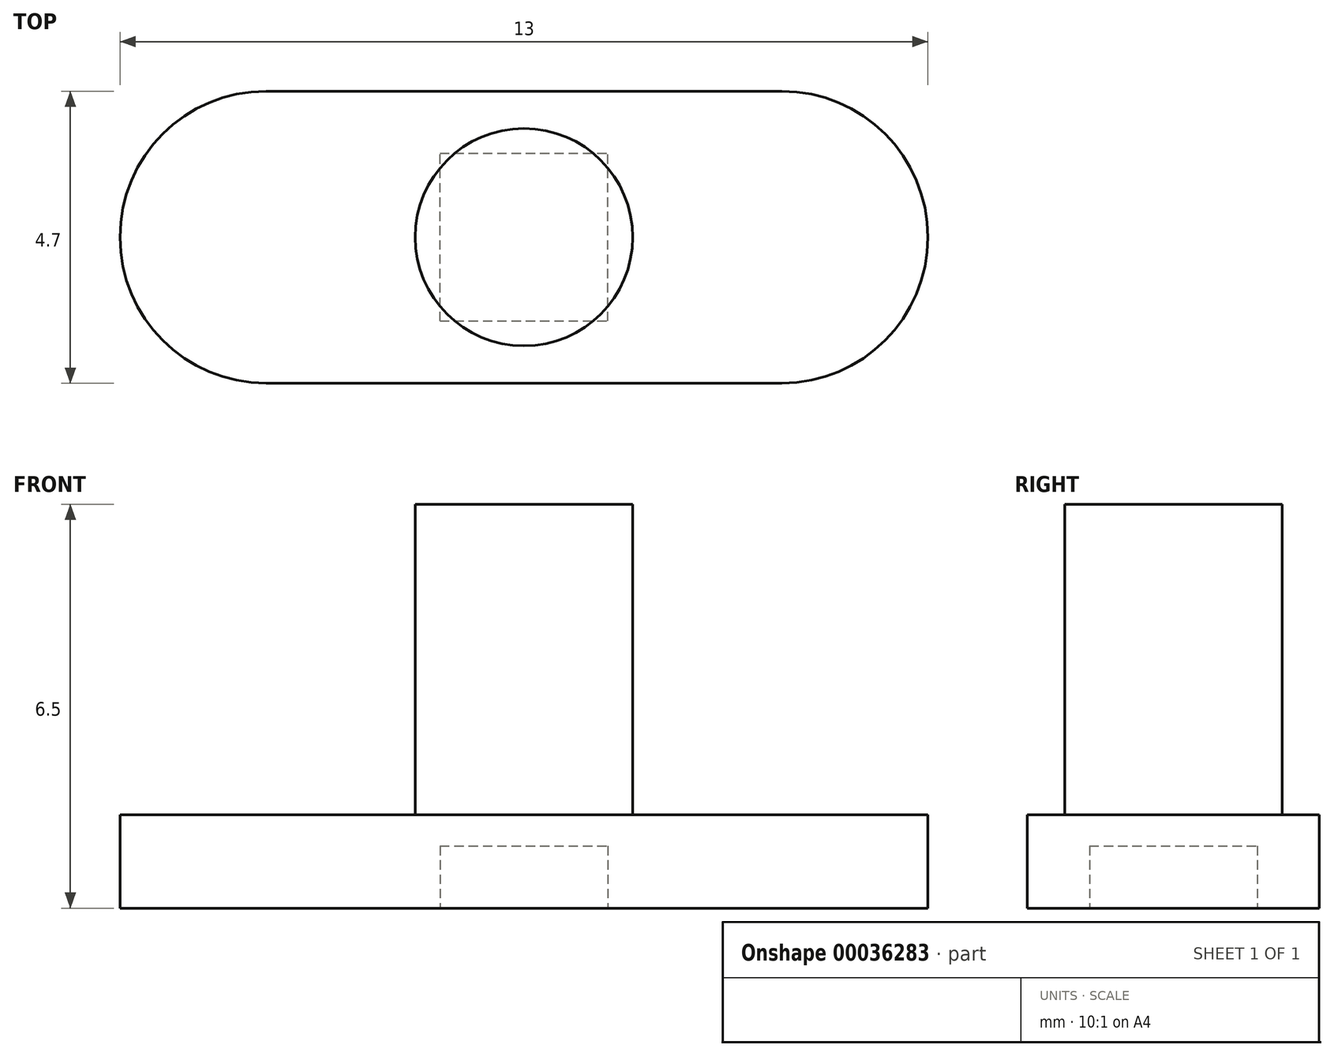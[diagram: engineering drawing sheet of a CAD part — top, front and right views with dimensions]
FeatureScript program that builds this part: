
annotation { "Feature Type Name" : "Feature", "Feature Type Description" : "" }
export const myFeature = defineFeature(function(context is Context, id is Id, definition is map)
    precondition{}
    {
        {
            var Q0;
            Q0=qCreatedBy(makeId("Top.planeOp"),FACE);
            var sketch = newSketch(context, id + "F0", { "sketchPlane" : qUnion([Q0])});
            skLineSegment(sketch, "E0.bottom", {"start": v(-0.65, 0) * mm, "end": v(7.65, 0) * mm});
            skLineSegment(sketch, "E0.top", {"start": v(-0.65, -4.7) * mm, "end": v(7.65, -4.7) * mm});
            skLineSegment(sketch, "E0.left", {"start": v(-0.65, 0) * mm, "end": v(-0.65, -4.7) * mm});
            skLineSegment(sketch, "E0.right", {"start": v(7.65, 0) * mm, "end": v(7.65, -4.7) * mm});
            skCircle(sketch, "E1", {"center": v(-0.65, -2.35) * mm, "radius": 2.35 * mm});
            skCircle(sketch, "E2", {"center": v(7.65, -2.35) * mm, "radius": 2.35 * mm});
            skLineSegment(sketch, "E3", {"start": v(-3, -2.35) * mm, "end": v(-0.65, -2.35) * mm, "construction": true});
            skLineSegment(sketch, "E4", {"start": v(-0.65, -2.35) * mm, "end": v(1.7, -2.35) * mm, "construction": true});
            skLineSegment(sketch, "E5", {"start": v(1.7, -2.35) * mm, "end": v(5.3, -2.35) * mm, "construction": true});
            skLineSegment(sketch, "E6", {"start": v(5.3, -2.35) * mm, "end": v(7.65, -2.35) * mm, "construction": true});
            skLineSegment(sketch, "E7", {"start": v(7.65, -2.35) * mm, "end": v(10, -2.35) * mm, "construction": true});
            skLineSegment(sketch, "E8", {"start": v(3.5, 0) * mm, "end": v(3.5, -2.35) * mm, "construction": true});
            skLineSegment(sketch, "E9", {"start": v(3.5, -4.7) * mm, "end": v(3.5, -2.35) * mm, "construction": true});
            skSolve(sketch);
        }
        {
            var Q0;
            {var subQ1=sQuery(id+"F0.wireOp",EDGE,"E0.left");Q0=makeQuery(id+"F0.imprint","IMPRINT",FACE,{"disambiguationData":[TD([[makeQuery(id+"F0.imprint","IMPRINT",EDGE,{"derivedFrom":subQ1}),-1.0]])]});}
            var Q1;
            {var subQ1=sQuery(id+"F0.wireOp",EDGE,"E0.left");Q1=makeQuery(id+"F0.imprint","IMPRINT",FACE,{"disambiguationData":[TD([[makeQuery(id+"F0.imprint","IMPRINT",EDGE,{"derivedFrom":subQ1}),1.0]])]});}
            var Q2;
            {var subQ3=sQuery(id+"F0.wireOp",EDGE,"E0.bottom");Q2=makeQuery(id+"F0.imprint","IMPRINT",FACE,{"disambiguationData":[TD([[makeQuery(id+"F0.imprint","IMPRINT",EDGE,{"derivedFrom":subQ3}),-1.0]])]});}
            var Q3;
            {var subQ1=sQuery(id+"F0.wireOp",EDGE,"E0.right");Q3=makeQuery(id+"F0.imprint","IMPRINT",FACE,{"disambiguationData":[TD([[makeQuery(id+"F0.imprint","IMPRINT",EDGE,{"derivedFrom":subQ1}),1.0]])]});}
            var Q4;
            {var subQ1=sQuery(id+"F0.wireOp",EDGE,"E0.right");Q4=makeQuery(id+"F0.imprint","IMPRINT",FACE,{"disambiguationData":[TD([[makeQuery(id+"F0.imprint","IMPRINT",EDGE,{"derivedFrom":subQ1}),-1.0]])]});}
            extrude(context, id + "F1", {"entities" : qUnion([Q0, Q1, Q2, Q3, Q4]), "depth" : 1.5 * mm});
        }
        {
            var Q0;
            Q0=makeQuery(id+"F1.opExtrude","CAP_FACE",FACE,{"disambiguationData":[OSD([sQuery(id+"F0.wireOp",EDGE,"E0.bottom"),sQuery(id+"F0.wireOp",EDGE,"E0.top"),sQuery(id+"F0.wireOp",EDGE,"E1"),sQuery(id+"F0.wireOp",EDGE,"E2")])],"isStart":false});
            var sketch = newSketch(context, id + "F2", { "sketchPlane" : qUnion([Q0])});
            skLineSegment(sketch, "E10", {"start": v(-3, -2.35) * mm, "end": v(10, -2.35) * mm, "construction": true});
            skLineSegment(sketch, "E11", {"start": v(3.5, 0) * mm, "end": v(3.5, -2.35) * mm, "construction": true});
            skLineSegment(sketch, "E12", {"start": v(3.5, -2.35) * mm, "end": v(3.5, -4.7) * mm, "construction": true});
            skCircle(sketch, "E13", {"center": v(3.5, -2.35) * mm, "radius": 1.75 * mm});
            skSolve(sketch);
        }
        {
            var Q0;
            Q0=makeQuery(id+"F2.imprint","IMPRINT",FACE,{"disambiguationData":[TD([[makeQuery(id+"F2.imprint","IMPRINT",EDGE,{"derivedFrom":sQuery(id+"F2.wireOp",EDGE,"E13")}),1.0]])]});
            extrude(context, id + "F3", {"entities" : qUnion([Q0]), "operationType" : NewBodyOperationType.ADD, "depth" : 5 * mm});
        }
        {
            var Q0;
            Q0=makeQuery(id+"F1.opExtrude","CAP_FACE",FACE,{"disambiguationData":[OSD([sQuery(id+"F0.wireOp",EDGE,"E0.bottom"),sQuery(id+"F0.wireOp",EDGE,"E0.top"),sQuery(id+"F0.wireOp",EDGE,"E1"),sQuery(id+"F0.wireOp",EDGE,"E2")])],"isStart":true});
            var sketch = newSketch(context, id + "F4", { "sketchPlane" : qUnion([Q0])});
            skLineSegment(sketch, "E14", {"start": v(-3, 2.35) * mm, "end": v(10, 2.35) * mm, "construction": true});
            skLineSegment(sketch, "E15", {"start": v(3.5, 4.7) * mm, "end": v(3.5, 2.35) * mm, "construction": true});
            skLineSegment(sketch, "E16", {"start": v(3.5, 2.35) * mm, "end": v(3.5, 0) * mm, "construction": true});
            skLineSegment(sketch, "E17.bottom", {"start": v(2.15, 3.7) * mm, "end": v(4.85, 3.7) * mm});
            skLineSegment(sketch, "E17.top", {"start": v(2.15, 1) * mm, "end": v(4.85, 1) * mm});
            skLineSegment(sketch, "E17.left", {"start": v(2.15, 3.7) * mm, "end": v(2.15, 1) * mm});
            skLineSegment(sketch, "E17.right", {"start": v(4.85, 3.7) * mm, "end": v(4.85, 1) * mm});
            skLineSegment(sketch, "E18", {"start": v(4.85, 2.35) * mm, "end": v(2.15, 2.35) * mm, "construction": true});
            skLineSegment(sketch, "E19", {"start": v(3.5, 3.7) * mm, "end": v(3.5, 2.35) * mm, "construction": true});
            skLineSegment(sketch, "E20", {"start": v(3.5, 2.35) * mm, "end": v(3.5, 1) * mm, "construction": true});
            skSolve(sketch);
        }
        {
            var Q0;
            Q0=makeQuery(id+"F4.imprint","IMPRINT",FACE,{"disambiguationData":[TD([[makeQuery(id+"F4.imprint","IMPRINT",EDGE,{"derivedFrom":sQuery(id+"F4.wireOp",EDGE,"E17.bottom")}),-1.0]])]});
            extrude(context, id + "F5", {"entities" : qUnion([Q0]), "operationType" : NewBodyOperationType.REMOVE, "oppositeDirection" : true, "depth" : 1 * mm});
        }
    });
